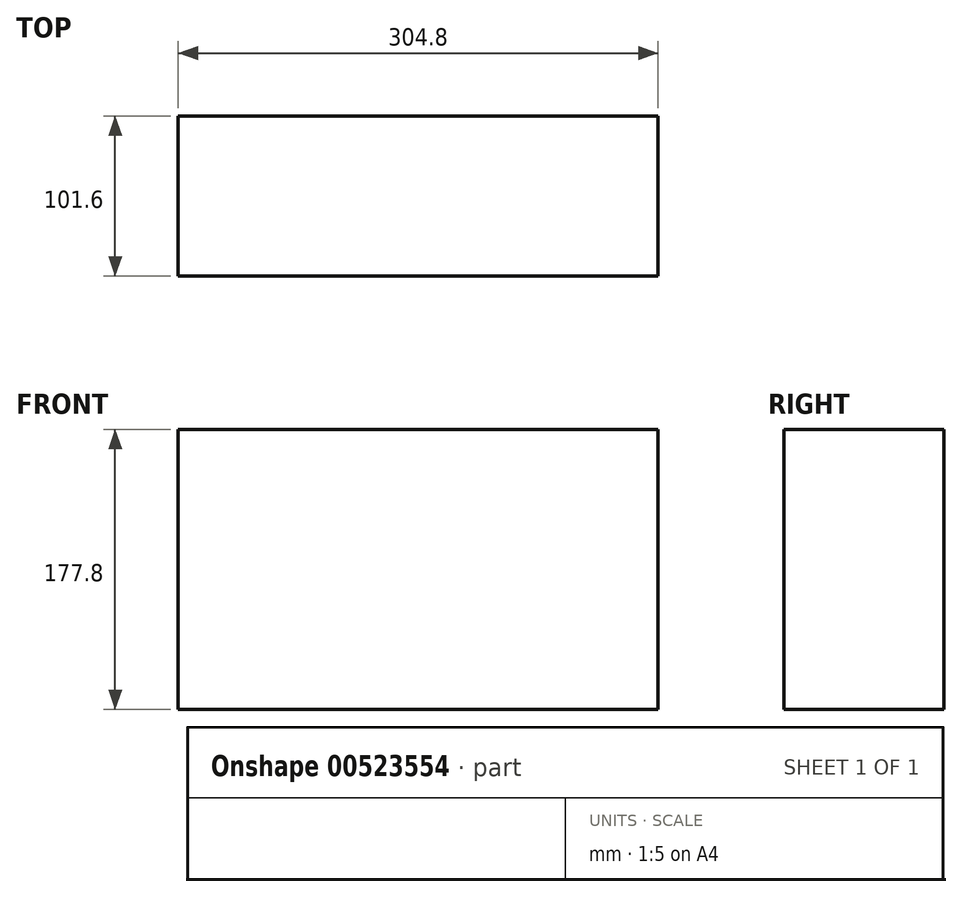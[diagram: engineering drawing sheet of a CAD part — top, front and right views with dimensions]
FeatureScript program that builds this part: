
annotation { "Feature Type Name" : "Feature", "Feature Type Description" : "" }
export const myFeature = defineFeature(function(context is Context, id is Id, definition is map)
    precondition{}
    {
        {
            var Q0;
            Q0=qCreatedBy(makeId("Front.planeOp"),FACE);
            var sketch = newSketch(context, id + "F0", { "sketchPlane" : qUnion([Q0])});
            skLineSegment(sketch, "E0", {"start": v(-141.98, 94.67) * mm, "end": v(162.82, 94.67) * mm});
            skLineSegment(sketch, "E1", {"start": v(162.82, 94.67) * mm, "end": v(162.82, -83.13) * mm});
            skLineSegment(sketch, "E2", {"start": v(162.82, -83.13) * mm, "end": v(-141.98, -83.13) * mm});
            skLineSegment(sketch, "E3", {"start": v(-141.98, 94.67) * mm, "end": v(-141.98, -83.13) * mm});
            skSolve(sketch);
        }
        {
            var Q0;
            Q0 = qSketchRegion(id + "F0", true);
            extrude(context, id + "F1", {"entities" : qUnion([Q0]), "depth" : 101.6 * mm, "offsetDistance" : 25.4 * mm});
        }
    });
